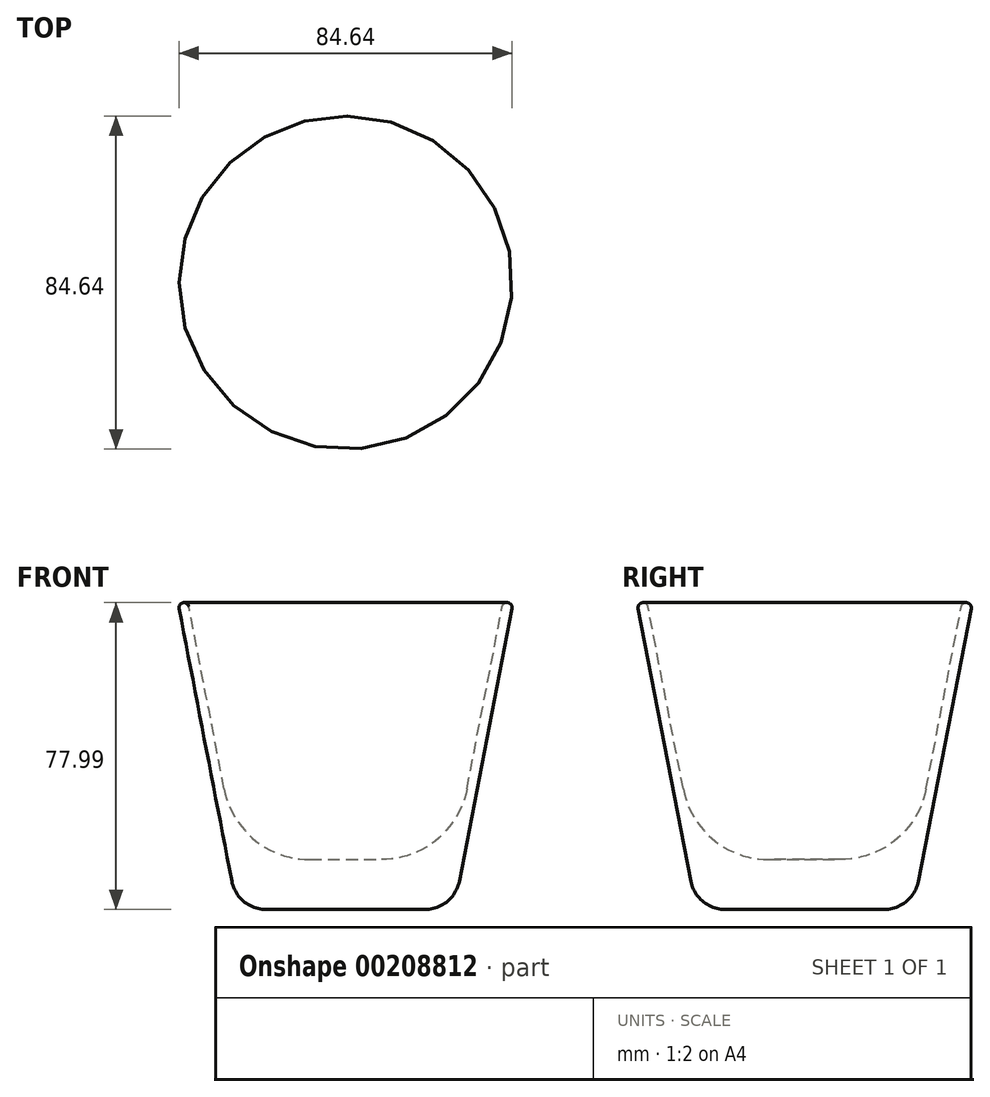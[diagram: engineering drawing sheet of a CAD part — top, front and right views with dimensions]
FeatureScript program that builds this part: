
annotation { "Feature Type Name" : "Feature", "Feature Type Description" : "" }
export const myFeature = defineFeature(function(context is Context, id is Id, definition is map)
    precondition{}
    {
        {
            var Q0;
            Q0=qCreatedBy(makeId("Front.planeOp"),FACE);
            var sketch = newSketch(context, id + "F0", { "sketchPlane" : qUnion([Q0])});
            skLineSegment(sketch, "E0", {"start": v(0, 0) * mm, "end": v(0, 76.2) * mm, "construction": true});
            skLineSegment(sketch, "E1", {"start": v(30.84, 28.1) * mm, "end": v(39.8, 74.42) * mm});
            skPoint(sketch, "E2.visualSharp", {"position": v(25.4, 0) * mm});
            skLineSegment(sketch, "E3.0", {"start": v(28.89, 4.66) * mm, "end": v(42.3, 73.94) * mm});
            skArc(sketch, "E3.1", {"start": v(20.16, -2.54) * mm, "mid": v(25.82, -0.5) * mm, "end": v(28.89, 4.66) * mm});
            skLineSegment(sketch, "E3.2", {"start": v(0, -2.54) * mm, "end": v(20.16, -2.54) * mm});
            skLineSegment(sketch, "E4.0", {"start": v(0, 10.16) * mm, "end": v(9.08, 10.16) * mm});
            skArc(sketch, "E5.filletArc", {"start": v(9.08, 10.16) * mm, "mid": v(23.19, 15.23) * mm, "end": v(30.84, 28.1) * mm});
            skPoint(sketch, "E6.orphan", {"position": v(40.15, 76.2) * mm});
            skArc(sketch, "E7", {"start": v(42.3, 73.94) * mm, "mid": v(41.3, 75.43) * mm, "end": v(39.8, 74.42) * mm});
            skLineSegment(sketch, "E8", {"start": v(0, 10.16) * mm, "end": v(0, -2.54) * mm});
            skSolve(sketch);
        }
        {
            var Q0;
            Q0=makeQuery(id+"F0.imprint","IMPRINT",FACE,{"disambiguationData":[TD([[makeQuery(id+"F0.imprint","IMPRINT",EDGE,{"derivedFrom":sQuery(id+"F0.wireOp",EDGE,"E1")}),-1.0]])]});
            var Q1;
            Q1=sQuery(id+"F0.wireOp",EDGE,"E0");
            revolve(context, id + "F1", {"entities" : qUnion([Q0]), "axis" : qUnion([Q1]), "revolveType" : RevolveType.FULL});
        }
    });
